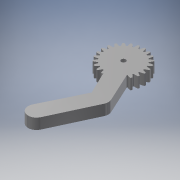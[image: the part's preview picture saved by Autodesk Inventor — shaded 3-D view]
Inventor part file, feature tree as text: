
AUTODESK INVENTOR PART (.ipt)
format: ipt  version: 2017 (Build 210142000, 142)  size: 268,800 bytes
history: native  units: mm (DEFAULTED — no unit token found)
features: sketch x5, extrude x4, plane x3, other x3
ambient origin geometry x8: Origin, YZ Plane, XZ Plane, XY Plane, X Axis, Y Axis, Z Axis, Center Point
bodies: Solid1 (feature_tree)
feature tree (15):
  extrude  "Extrusion1"  Depth=8.0mm TaperAngle=0.0deg
  plane  "Work Plane2"
  plane  "Work Plane8"
  plane  "Work Plane9"
  other  "Spur Gear"
  extrude  "Extrusion2"  Depth=10.0mm TaperAngle=0.0deg
  extrude  "Extrusion3"  Depth=1.308997mm TaperAngle=0.0deg
  extrude  "Extrusion4"  TaperAngle=0.0deg  [1 undecoded]
  sketch  "Sketch1"  dims[d0=32.5mm d1=8.0mm d2=0.0mm]
  sketch  "Sketch2"  dims[d3=30.0mm d4=10.0mm d5=0.0mm]
  other  "Srf1"
  sketch  "Sketch3"  dims[d16=30.0mm d17=0.0mm d34=1.308997mm]
  sketch  "Sketch4"  dims[d39=0.0mm d41=0.0mm]
  sketch  "Sketch5"  dims[d43=30.0mm d46=30.0mm d47=0.0mm d48=0.0mm d49=3.4544mm d50=10.0mm d51=0.0mm d52=10.0838mm d53=3.0mm d54=0.0mm d57=12.5mm d59=12.5mm d60=12.5mm d61=8.0mm d62=0.0mm]
  other  "Pitch Diameter"
note: 1 required parameter value undecoded (feature->parameter linkage not recoverable at this tier; creation-order binding heuristic only, values carry confidence <= 0.55)
